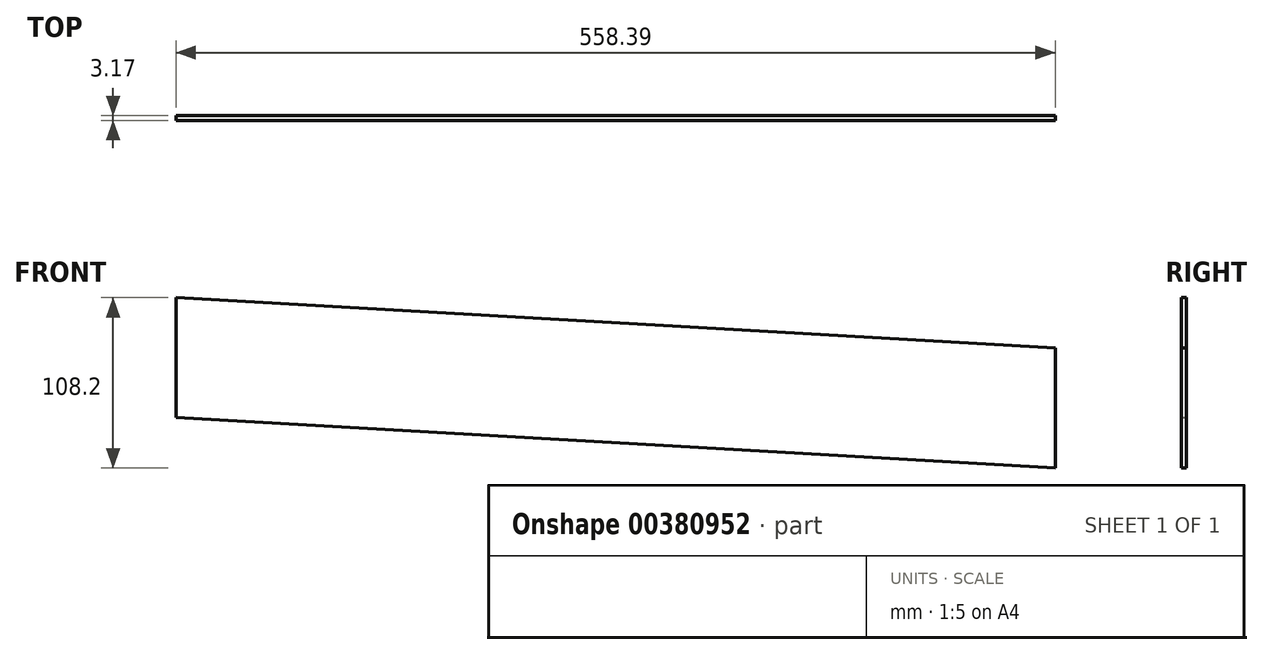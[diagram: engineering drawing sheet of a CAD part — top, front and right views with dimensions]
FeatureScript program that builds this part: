
annotation { "Feature Type Name" : "Feature", "Feature Type Description" : "" }
export const myFeature = defineFeature(function(context is Context, id is Id, definition is map)
    precondition{}
    {
        {
            var Q0;
            Q0=qCreatedBy(makeId("Front.planeOp"),FACE);
            var sketch = newSketch(context, id + "F0", { "sketchPlane" : qUnion([Q0])});
            skLineSegment(sketch, "E0", {"start": v(0, 0) * mm, "end": v(0, 76.2) * mm});
            skLineSegment(sketch, "E1", {"start": v(0, 76.2) * mm, "end": v(-558.4, 108.2) * mm});
            skLineSegment(sketch, "E2", {"start": v(-558.4, 108.2) * mm, "end": v(-558.4, 32) * mm});
            skLineSegment(sketch, "E3", {"start": v(-558.4, 32) * mm, "end": v(0, 0) * mm});
            skSolve(sketch);
        }
        {
            var Q0;
            Q0=qSketchRegion(id+"F0",true);
            extrude(context, id + "F1", {"entities" : qUnion([Q0]), "depth" : 3.17 * mm});
        }
    });
